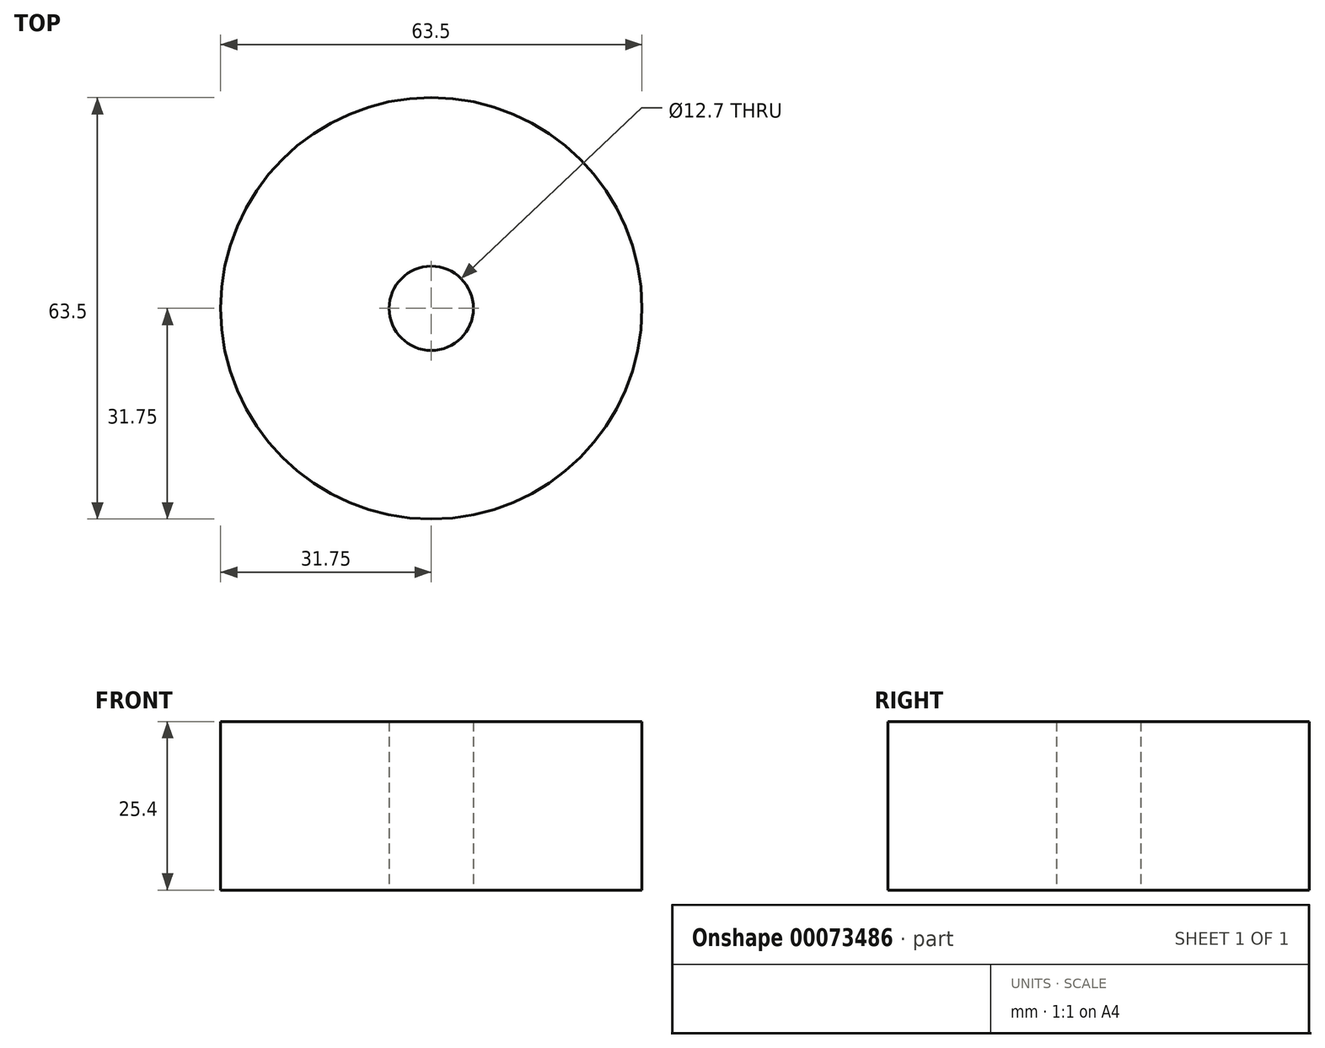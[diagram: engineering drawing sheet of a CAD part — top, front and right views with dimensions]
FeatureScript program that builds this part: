
annotation { "Feature Type Name" : "Feature", "Feature Type Description" : "" }
export const myFeature = defineFeature(function(context is Context, id is Id, definition is map)
    precondition{}
    {
        {
            var Q0;
            Q0=qCreatedBy(makeId("Top.planeOp"),FACE);
            var sketch = newSketch(context, id + "F0", { "sketchPlane" : qUnion([Q0])});
            skCircle(sketch, "E0", {"center": v(0, 0) * mm, "radius": 31.75 * mm});
            skCircle(sketch, "E1", {"center": v(0, 0) * mm, "radius": 6.35 * mm});
            skSolve(sketch);
        }
        {
            var Q0;
            Q0=makeQuery(id+"F0.imprint","IMPRINT",FACE,{"disambiguationData":[TD([[makeQuery(id+"F0.imprint","IMPRINT",EDGE,{"derivedFrom":sQuery(id+"F0.wireOp",EDGE,"E0")}),1.0]])]});
            extrude(context, id + "F1", {"entities" : qUnion([Q0]), "depth" : 25.4 * mm});
        }
    });
